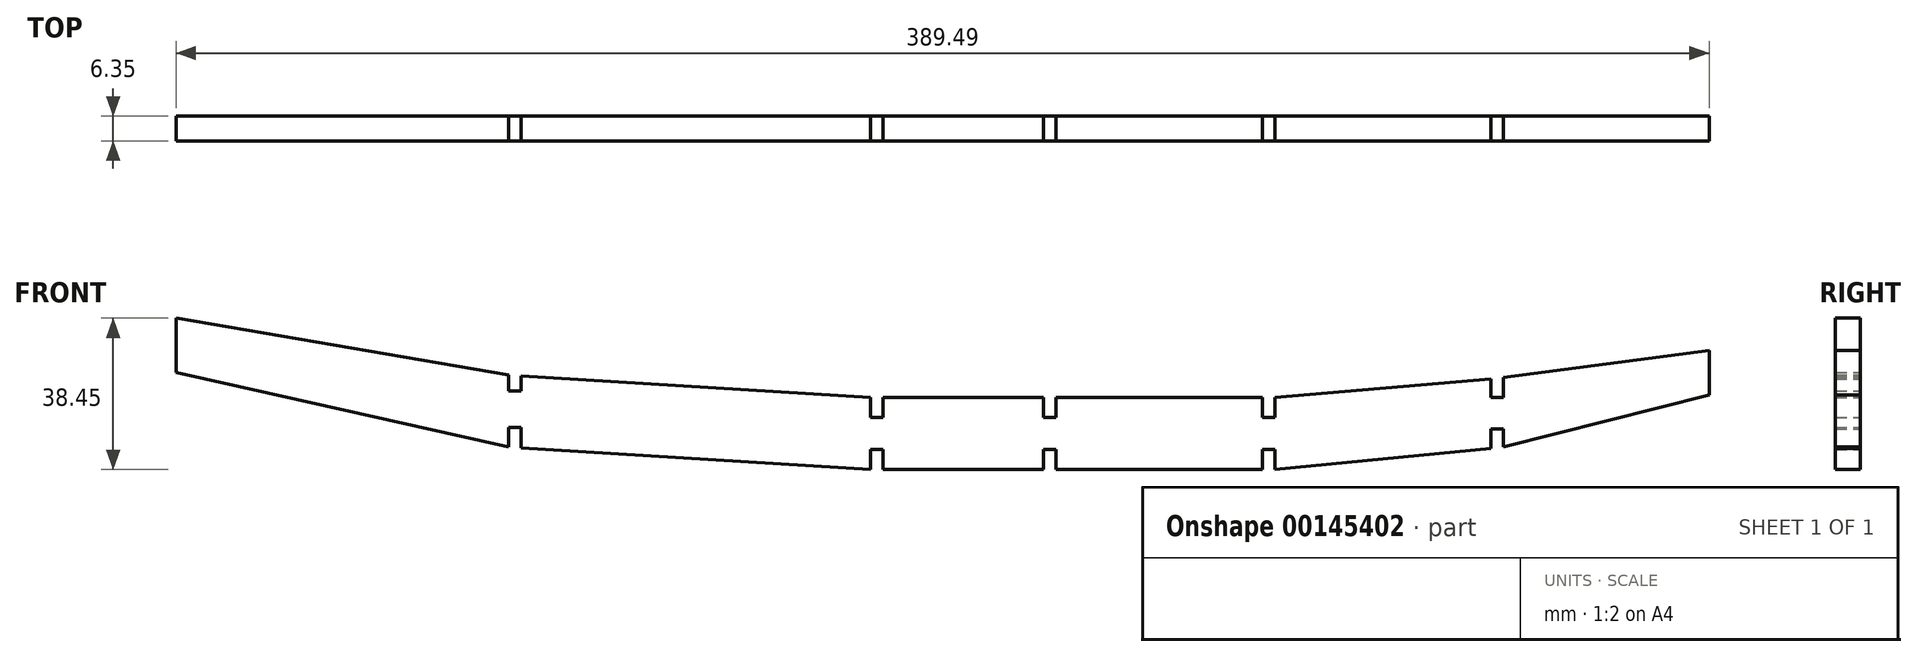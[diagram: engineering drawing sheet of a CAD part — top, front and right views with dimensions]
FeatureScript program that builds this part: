
annotation { "Feature Type Name" : "Feature", "Feature Type Description" : "" }
export const myFeature = defineFeature(function(context is Context, id is Id, definition is map)
    precondition{}
    {
        {
            var Q0;
            Q0=qCreatedBy(makeId("Front.planeOp"),FACE);
            var sketch = newSketch(context, id + "F0", { "sketchPlane" : qUnion([Q0])});
            skLineSegment(sketch, "E0", {"start": v(-220.35, 53.21) * mm, "end": v(-135.9, 38.72) * mm});
            skLineSegment(sketch, "E1", {"start": v(-132.73, 38.52) * mm, "end": v(-43.88, 33.04) * mm});
            skLineSegment(sketch, "E2", {"start": v(-40.7, 33.04) * mm, "end": v(0, 33.04) * mm});
            skLineSegment(sketch, "E3", {"start": v(3.18, 33.04) * mm, "end": v(55.67, 33.04) * mm});
            skLineSegment(sketch, "E4", {"start": v(58.84, 33.04) * mm, "end": v(113.65, 37.8) * mm});
            skLineSegment(sketch, "E5", {"start": v(116.83, 38.09) * mm, "end": v(169.14, 45.02) * mm});
            skLineSegment(sketch, "E6", {"start": v(169.14, 45.02) * mm, "end": v(169.14, 33.67) * mm});
            skLineSegment(sketch, "E7", {"start": v(169.14, 33.67) * mm, "end": v(116.83, 20.44) * mm});
            skLineSegment(sketch, "E8", {"start": v(113.65, 20.13) * mm, "end": v(58.84, 14.76) * mm});
            skLineSegment(sketch, "E9", {"start": v(55.67, 14.76) * mm, "end": v(3.18, 14.76) * mm});
            skLineSegment(sketch, "E10", {"start": v(0, 14.76) * mm, "end": v(-40.7, 14.76) * mm});
            skLineSegment(sketch, "E11", {"start": v(-43.88, 14.76) * mm, "end": v(-132.73, 20.24) * mm});
            skLineSegment(sketch, "E12", {"start": v(-135.9, 20.44) * mm, "end": v(-220.35, 39.35) * mm});
            skLineSegment(sketch, "E13", {"start": v(-220.35, 53.21) * mm, "end": v(-220.35, 39.35) * mm});
            skLineSegment(sketch, "E14.left", {"start": v(-135.9, 38.72) * mm, "end": v(-135.9, 34.66) * mm});
            skLineSegment(sketch, "E14.right", {"start": v(-132.73, 38.72) * mm, "end": v(-132.73, 34.66) * mm});
            skLineSegment(sketch, "E15.left", {"start": v(-43.88, 33.04) * mm, "end": v(-43.88, 27.96) * mm});
            skLineSegment(sketch, "E15.right", {"start": v(-40.7, 33.04) * mm, "end": v(-40.7, 27.96) * mm});
            skLineSegment(sketch, "E16.left", {"start": v(0, 33.04) * mm, "end": v(0, 27.96) * mm});
            skLineSegment(sketch, "E16.right", {"start": v(3.18, 33.04) * mm, "end": v(3.18, 27.96) * mm});
            skLineSegment(sketch, "E17.left", {"start": v(58.84, 33.04) * mm, "end": v(58.84, 27.96) * mm});
            skLineSegment(sketch, "E17.right", {"start": v(55.67, 33.04) * mm, "end": v(55.67, 27.96) * mm});
            skLineSegment(sketch, "E18.left", {"start": v(116.83, 38.09) * mm, "end": v(116.83, 33.07) * mm});
            skLineSegment(sketch, "E18.right", {"start": v(113.65, 37.8) * mm, "end": v(113.65, 33.07) * mm});
            skLineSegment(sketch, "E19", {"start": v(113.65, 33.07) * mm, "end": v(116.83, 33.07) * mm});
            skLineSegment(sketch, "E20", {"start": v(113.65, 25.05) * mm, "end": v(116.83, 25.05) * mm});
            skLineSegment(sketch, "E21", {"start": v(-135.9, 34.66) * mm, "end": v(-132.73, 34.66) * mm});
            skLineSegment(sketch, "E22", {"start": v(-135.9, 25.42) * mm, "end": v(-132.73, 25.42) * mm});
            skLineSegment(sketch, "E23", {"start": v(-43.88, 27.96) * mm, "end": v(-40.7, 27.96) * mm});
            skLineSegment(sketch, "E24.bottom", {"start": v(-43.88, 19.27) * mm, "end": v(-40.7, 19.27) * mm});
            skLineSegment(sketch, "E24.top", {"start": v(-43.88, 19.84) * mm, "end": v(-40.7, 19.84) * mm});
            skLineSegment(sketch, "E24.left", {"start": v(-43.88, 19.27) * mm, "end": v(-43.88, 19.84) * mm});
            skLineSegment(sketch, "E24.right", {"start": v(-40.7, 19.27) * mm, "end": v(-40.7, 19.84) * mm});
            skLineSegment(sketch, "E25", {"start": v(0, 27.96) * mm, "end": v(3.18, 27.96) * mm});
            skLineSegment(sketch, "E26", {"start": v(0, 19.84) * mm, "end": v(3.18, 19.84) * mm});
            skLineSegment(sketch, "E27", {"start": v(55.67, 19.84) * mm, "end": v(58.84, 19.84) * mm});
            skLineSegment(sketch, "E28", {"start": v(55.67, 27.96) * mm, "end": v(58.84, 27.96) * mm});
            skLineSegment(sketch, "E29.trimOffspring", {"start": v(-135.9, 25.42) * mm, "end": v(-135.9, 20.44) * mm});
            skLineSegment(sketch, "E30.trimOffspring", {"start": v(-132.73, 25.42) * mm, "end": v(-132.73, 20.24) * mm});
            skLineSegment(sketch, "E31.trimOffspring", {"start": v(-43.88, 19.84) * mm, "end": v(-43.88, 14.76) * mm});
            skLineSegment(sketch, "E32.trimOffspring", {"start": v(-40.7, 19.84) * mm, "end": v(-40.7, 14.76) * mm});
            skLineSegment(sketch, "E33.trimOffspring", {"start": v(0, 19.84) * mm, "end": v(0, 14.76) * mm});
            skLineSegment(sketch, "E34.trimOffspring", {"start": v(3.18, 19.84) * mm, "end": v(3.18, 14.76) * mm});
            skLineSegment(sketch, "E35.trimOffspring", {"start": v(55.67, 19.84) * mm, "end": v(55.67, 14.76) * mm});
            skLineSegment(sketch, "E36.trimOffspring", {"start": v(58.84, 19.84) * mm, "end": v(58.84, 14.76) * mm});
            skLineSegment(sketch, "E37.trimOffspring", {"start": v(113.65, 25.05) * mm, "end": v(113.65, 20.13) * mm});
            skLineSegment(sketch, "E38.trimOffspring", {"start": v(116.83, 25.05) * mm, "end": v(116.83, 20.44) * mm});
            skSolve(sketch);
        }
        {
            var Q0;
            Q0=makeQuery(id+"F0.imprint","IMPRINT",FACE,{"disambiguationData":[TD([[makeQuery(id+"F0.imprint","IMPRINT",EDGE,{"derivedFrom":sQuery(id+"F0.wireOp",EDGE,"E0")}),-1.0]])]});
            extrude(context, id + "F1", {"entities" : qUnion([Q0]), "depth" : 6.35 * mm});
        }
    });
